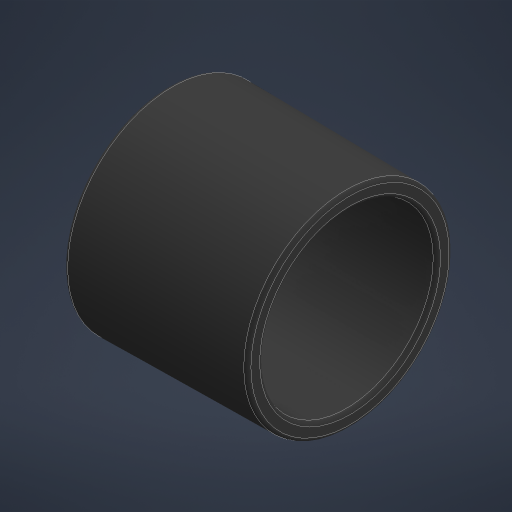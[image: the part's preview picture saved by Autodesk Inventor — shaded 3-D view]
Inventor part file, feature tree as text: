
AUTODESK INVENTOR PART (.ipt)
format: ipt  version: 2024.1 (Build 281209000, 209)  size: 214,016 bytes
history: native  units: mm
features: revolve x1, sketch x1
ambient origin geometry x8: Origin, YZ Plane, XZ Plane, XY Plane, X Axis, Y Axis, Z Axis, Center Point
bodies: Solid1 (feature_tree)
feature tree (2):
  revolve  "Revolution1"  [1 undecoded]
  sketch  "Sketch1"  dims[d0=13.0mm d1=11.0mm d2=6.0mm d3=1.1mm d5=2.0mm d6=7.25mm d7=60.0mm d8=0.5mm d9=0.25mm d10=90.0deg d11=0.872665mm]
note: 1 required parameter value undecoded (feature->parameter linkage not recoverable at this tier; creation-order binding heuristic only, values carry confidence <= 0.55)
